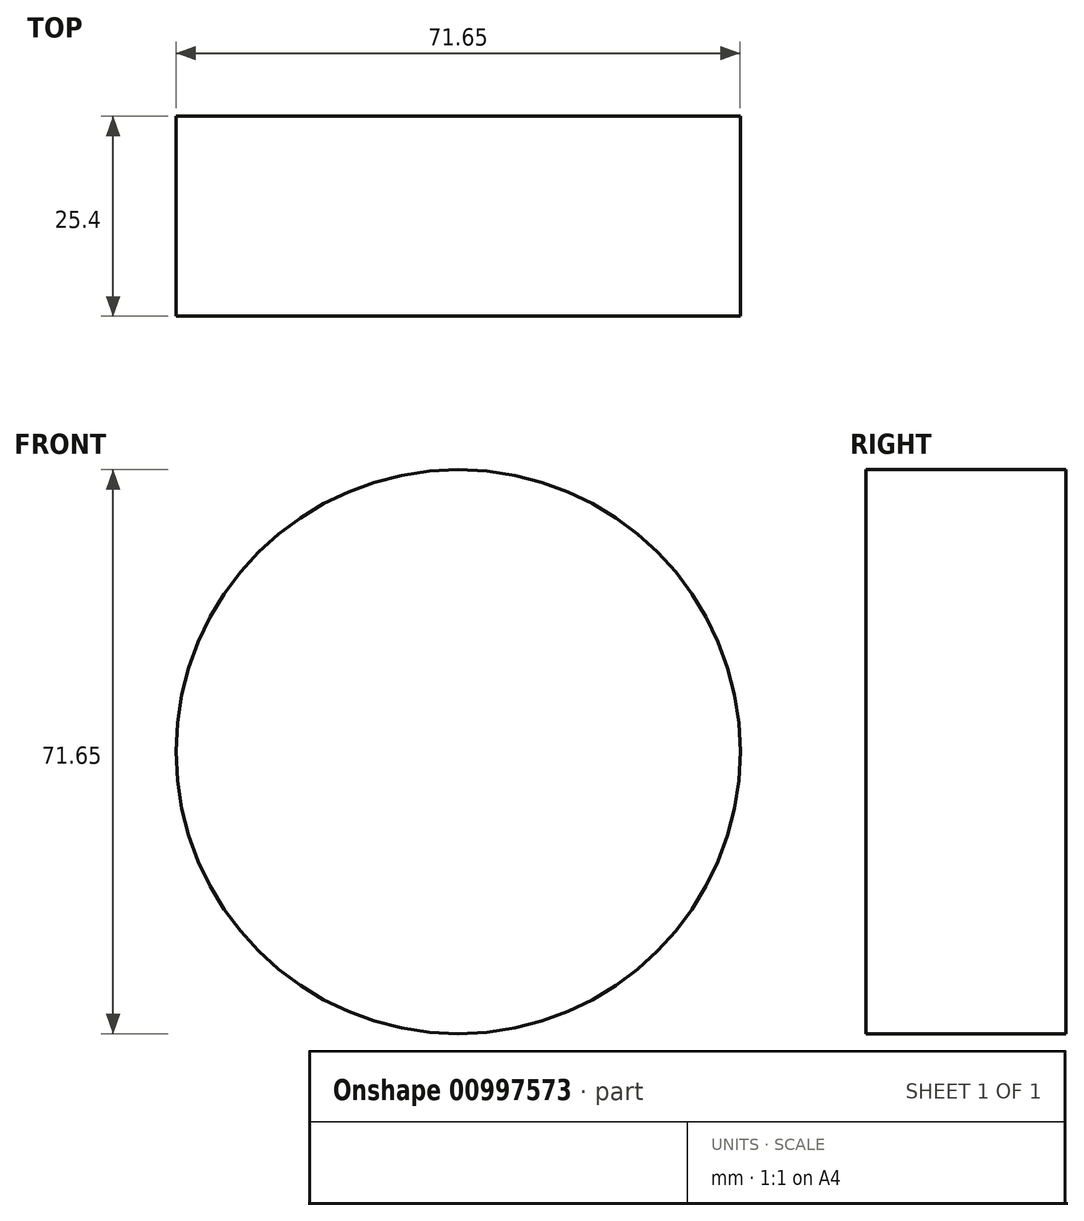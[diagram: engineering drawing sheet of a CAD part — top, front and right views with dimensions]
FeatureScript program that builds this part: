
annotation { "Feature Type Name" : "Feature", "Feature Type Description" : "" }
export const myFeature = defineFeature(function(context is Context, id is Id, definition is map)
    precondition{}
    {
        {
            var Q0;
            Q0=qCreatedBy(makeId("Front.planeOp"),FACE);
            var sketch = newSketch(context, id + "F0", { "sketchPlane" : qUnion([Q0])});
            skCircle(sketch, "E0", {"center": v(-69.06, 35.83) * mm, "radius": 35.83 * mm});
            skPoint(sketch, "E0.first.point", {"position": v(-104.16, 28.62) * mm});
            skPoint(sketch, "E0.second.point", {"position": v(-68.56, 0) * mm});
            skPoint(sketch, "E0.third.point", {"position": v(-37.19, 52.18) * mm});
            skSolve(sketch);
        }
        {
            var Q0;
            Q0=sQuery(id+"F0.wireOp",EDGE,"E0");
            extrude(context, id + "F1", {"bodyType" : ToolBodyType.SURFACE, "surfaceEntities" : qUnion([Q0]), "depth" : 25.4 * mm, "offsetDistance" : 25.4 * mm});
        }
    });
